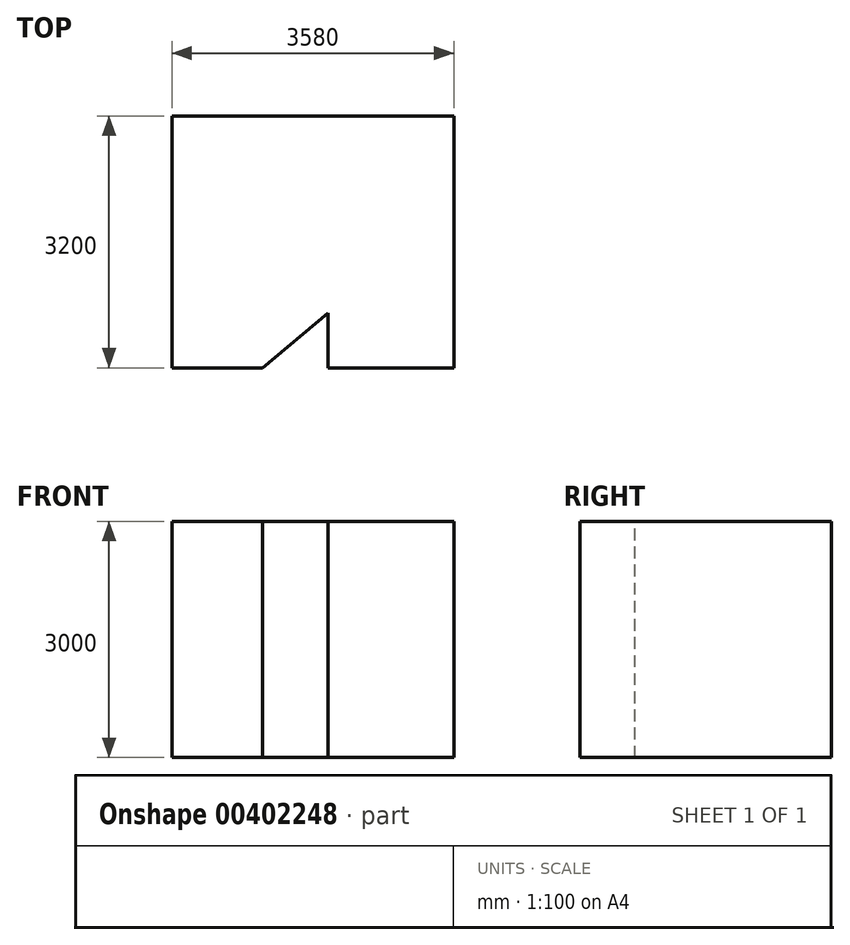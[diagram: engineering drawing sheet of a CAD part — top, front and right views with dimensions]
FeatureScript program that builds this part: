
annotation { "Feature Type Name" : "Feature", "Feature Type Description" : "" }
export const myFeature = defineFeature(function(context is Context, id is Id, definition is map)
    precondition{}
    {
        {
            var Q0;
            Q0=qCreatedBy(makeId("Top.planeOp"),FACE);
            var sketch = newSketch(context, id + "F0", { "sketchPlane" : qUnion([Q0])});
            skLineSegment(sketch, "E0", {"start": v(0, 0) * mm, "end": v(0, 3200) * mm});
            skLineSegment(sketch, "E1", {"start": v(0, 3200) * mm, "end": v(3580, 3200) * mm});
            skLineSegment(sketch, "E2", {"start": v(3580, 0) * mm, "end": v(1980, 0) * mm});
            skLineSegment(sketch, "E3", {"start": v(1980, 0) * mm, "end": v(1980, 700) * mm});
            skLineSegment(sketch, "E4", {"start": v(1980, 700) * mm, "end": v(1150, 0) * mm});
            skLineSegment(sketch, "E5", {"start": v(1150, 0) * mm, "end": v(0, 0) * mm});
            skLineSegment(sketch, "E6", {"start": v(3580, 3200) * mm, "end": v(3580, 2100) * mm});
            skLineSegment(sketch, "E7", {"start": v(3580, 2100) * mm, "end": v(3580, 0) * mm});
            skSolve(sketch);
        }
        {
            var Q0;
            Q0 = qSketchRegion(id + "F0", true);
            var Q1;
            Q1 = qConstructionFilter(qBodyType(qCreatedBy(id + "F0" ,EDGE), BodyType.WIRE), ConstructionObject.NO);
            extrude(context, id + "F1", {"entities" : qUnion([Q0]), "bodyType" : ToolBodyType.SURFACE, "surfaceEntities" : qUnion([Q1]), "depth" : 3000 * mm});
        }
    });
